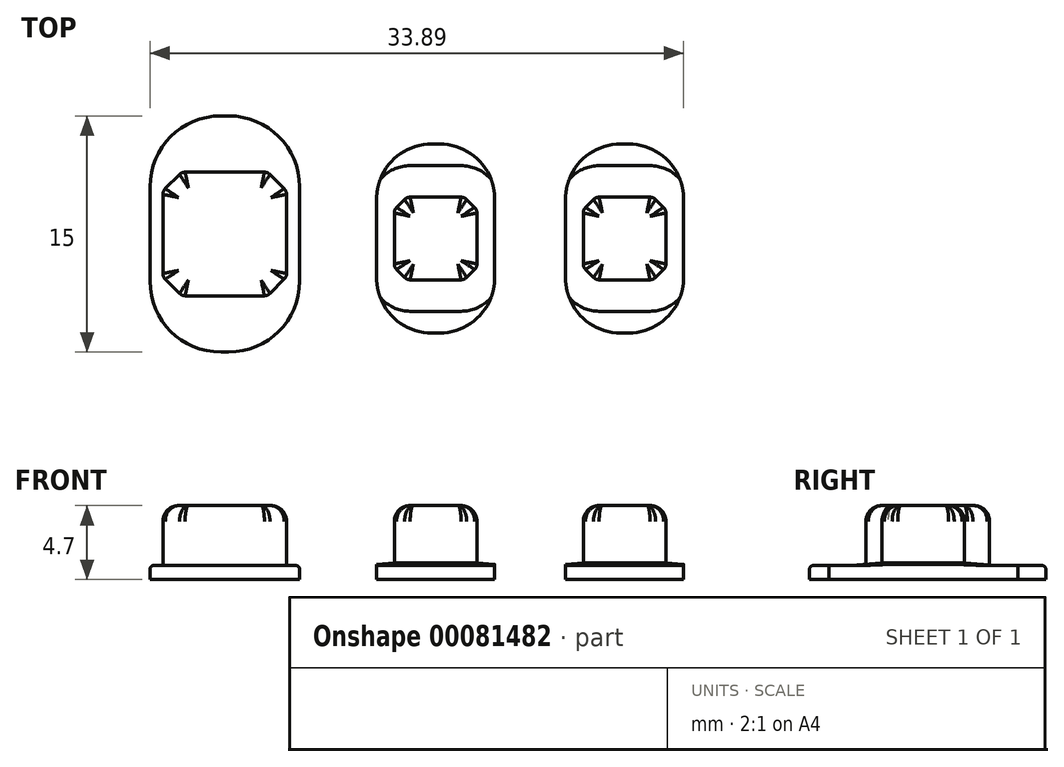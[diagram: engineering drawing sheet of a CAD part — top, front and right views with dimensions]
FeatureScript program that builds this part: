
annotation { "Feature Type Name" : "Feature", "Feature Type Description" : "" }
export const myFeature = defineFeature(function(context is Context, id is Id, definition is map)
    precondition{}
    {
        {
            var Q0;
            Q0=qCreatedBy(makeId("Top.planeOp"),FACE);
            var sketch = newSketch(context, id + "F0", { "sketchPlane" : qUnion([Q0])});
            skLineSegment(sketch, "E0.bottom", {"start": v(-23.44, 11.8) * mm, "end": v(-13.94, 11.8) * mm});
            skLineSegment(sketch, "E0.top", {"start": v(-23.44, -3.2) * mm, "end": v(-13.94, -3.2) * mm});
            skLineSegment(sketch, "E0.left", {"start": v(-23.44, 11.8) * mm, "end": v(-23.44, -3.2) * mm});
            skLineSegment(sketch, "E0.right", {"start": v(-13.94, 11.8) * mm, "end": v(-13.94, -3.2) * mm});
            skLineSegment(sketch, "E1.bottom", {"start": v(-9.05, 10) * mm, "end": v(-1.55, 10) * mm});
            skLineSegment(sketch, "E1.top", {"start": v(-9.05, -2) * mm, "end": v(-1.55, -2) * mm});
            skLineSegment(sketch, "E1.left", {"start": v(-9.05, 10) * mm, "end": v(-9.05, -2) * mm});
            skLineSegment(sketch, "E1.right", {"start": v(-1.55, 10) * mm, "end": v(-1.55, -2) * mm});
            skSolve(sketch);
        }
        {
            var Q0;
            Q0 = qSketchRegion(id + "F0", true);
            extrude(context, id + "F1", {"entities" : qUnion([Q0]), "depth" : .9 * mm});
        }
        {
            var Q0;
            Q0=makeQuery(id+"F1.opExtrude","CAP_FACE",FACE,{"disambiguationData":[OSD([sQuery(id+"F0.wireOp",EDGE,"E0.bottom"),sQuery(id+"F0.wireOp",EDGE,"E0.top"),sQuery(id+"F0.wireOp",EDGE,"E0.left"),sQuery(id+"F0.wireOp",EDGE,"E0.right")])],"isStart":false});
            var sketch = newSketch(context, id + "F2", { "sketchPlane" : qUnion([Q0])});
            skLineSegment(sketch, "E2", {"start": v(-23.44, 4.3) * mm, "end": v(-22.62, 4.3) * mm});
            skLineSegment(sketch, "E3.bottom", {"start": v(-22.62, 8.22) * mm, "end": v(-14.77, 8.22) * mm});
            skLineSegment(sketch, "E3.top", {"start": v(-22.62, 0.37) * mm, "end": v(-14.77, 0.37) * mm});
            skLineSegment(sketch, "E3.left", {"start": v(-22.62, 8.22) * mm, "end": v(-22.62, 0.37) * mm});
            skLineSegment(sketch, "E3.right", {"start": v(-14.77, 8.22) * mm, "end": v(-14.77, 0.37) * mm});
            skPoint(sketch, "E4", {"position": v(-18.7, 0.37) * mm});
            skPoint(sketch, "E5", {"position": v(-22.62, 4.3) * mm});
            skLineSegment(sketch, "E6.trimOffspring", {"start": v(-14.77, 4.3) * mm, "end": v(-13.94, 4.3) * mm});
            skPoint(sketch, "E7.orphan", {"position": v(-18.7, 4.3) * mm});
            skLineSegment(sketch, "E8", {"start": v(-18.7, 0.37) * mm, "end": v(-18.7, 4.3) * mm});
            skSolve(sketch);
        }
        {
            var Q0;
            Q0 = qSketchRegion(id + "F2", true);
            extrude(context, id + "F3", {"entities" : qUnion([Q0]), "operationType" : NewBodyOperationType.ADD, "depth" : 3.8 * mm});
        }
        {
            var Q0;
            Q0=makeQuery(id+"F1.opExtrude","CAP_FACE",FACE,{"disambiguationData":[OSD([sQuery(id+"F0.wireOp",EDGE,"E1.bottom"),sQuery(id+"F0.wireOp",EDGE,"E1.top"),sQuery(id+"F0.wireOp",EDGE,"E1.left"),sQuery(id+"F0.wireOp",EDGE,"E1.right")])],"isStart":false});
            var sketch = newSketch(context, id + "F4", { "sketchPlane" : qUnion([Q0])});
            skPoint(sketch, "E9", {"position": v(-5.3, 10) * mm});
            skPoint(sketch, "E10", {"position": v(-9.05, 4) * mm});
            skLineSegment(sketch, "E11.bottom", {"start": v(-7.92, 6.63) * mm, "end": v(-2.67, 6.63) * mm});
            skLineSegment(sketch, "E11.top", {"start": v(-7.92, 1.38) * mm, "end": v(-2.67, 1.38) * mm});
            skLineSegment(sketch, "E11.left", {"start": v(-7.92, 6.63) * mm, "end": v(-7.92, 1.38) * mm});
            skLineSegment(sketch, "E11.right", {"start": v(-2.67, 6.63) * mm, "end": v(-2.67, 1.38) * mm});
            skLineSegment(sketch, "E12", {"start": v(-9.05, 4) * mm, "end": v(-7.92, 4) * mm});
            skLineSegment(sketch, "E13", {"start": v(-5.3, 10) * mm, "end": v(-5.3, 6.63) * mm});
            skSolve(sketch);
        }
        {
            var Q0;
            Q0 = qSketchRegion(id + "F4", true);
            extrude(context, id + "F5", {"entities" : qUnion([Q0]), "operationType" : NewBodyOperationType.ADD, "depth" : 3.8 * mm});
        }
        {
            var Q0;
            Q0=makeQuery(id+"F1.opExtrude","SWEPT_EDGE",EDGE,{"disambiguationData":[OSD([sQuery(id+"F0.wireOp",EDGE,"E0.top"),sQuery(id+"F0.wireOp",EDGE,"E0.left")])]});
            var Q1;
            Q1=makeQuery(id+"F1.opExtrude","SWEPT_EDGE",EDGE,{"disambiguationData":[OSD([sQuery(id+"F0.wireOp",EDGE,"E0.top"),sQuery(id+"F0.wireOp",EDGE,"E0.right")])]});
            var Q2;
            Q2=makeQuery(id+"F1.opExtrude","SWEPT_EDGE",EDGE,{"disambiguationData":[OSD([sQuery(id+"F0.wireOp",EDGE,"E0.bottom"),sQuery(id+"F0.wireOp",EDGE,"E0.left")])]});
            var Q3;
            Q3=makeQuery(id+"F1.opExtrude","SWEPT_EDGE",EDGE,{"disambiguationData":[OSD([sQuery(id+"F0.wireOp",EDGE,"E0.bottom"),sQuery(id+"F0.wireOp",EDGE,"E0.right")])]});
            fillet(context, id + "F6", {"entities" : qUnion([Q0, Q1, Q2, Q3]), "radius" : 4.5 * mm, "tangentPropagation" : true, "allowEdgeOverflow" : false});
        }
        {
            var Q0;
            Q0=makeQuery(id+"F1.opExtrude","SWEPT_EDGE",EDGE,{"disambiguationData":[OSD([sQuery(id+"F0.wireOp",EDGE,"E1.bottom"),sQuery(id+"F0.wireOp",EDGE,"E1.left")])]});
            var Q1;
            Q1=makeQuery(id+"F1.opExtrude","SWEPT_EDGE",EDGE,{"disambiguationData":[OSD([sQuery(id+"F0.wireOp",EDGE,"E1.bottom"),sQuery(id+"F0.wireOp",EDGE,"E1.right")])]});
            var Q2;
            Q2=makeQuery(id+"F1.opExtrude","SWEPT_EDGE",EDGE,{"disambiguationData":[OSD([sQuery(id+"F0.wireOp",EDGE,"E1.top"),sQuery(id+"F0.wireOp",EDGE,"E1.left")])]});
            var Q3;
            Q3=makeQuery(id+"F1.opExtrude","SWEPT_EDGE",EDGE,{"disambiguationData":[OSD([sQuery(id+"F0.wireOp",EDGE,"E1.top"),sQuery(id+"F0.wireOp",EDGE,"E1.right")])]});
            fillet(context, id + "F7", {"entities" : qUnion([Q0, Q1, Q2, Q3]), "radius" : 3.5 * mm, "tangentPropagation" : true, "allowEdgeOverflow" : false});
        }
        {
            var Q0;
            Q0=makeQuery(id+"F3.opExtrude","SWEPT_EDGE",EDGE,{"disambiguationData":[OSD([sQuery(id+"F2.wireOp",EDGE,"E3.top"),sQuery(id+"F2.wireOp",EDGE,"E3.left")])]});
            var Q1;
            Q1=makeQuery(id+"F3.opExtrude","SWEPT_EDGE",EDGE,{"disambiguationData":[OSD([sQuery(id+"F2.wireOp",EDGE,"E3.top"),sQuery(id+"F2.wireOp",EDGE,"E3.right")])]});
            var Q2;
            Q2=makeQuery(id+"F3.opExtrude","SWEPT_EDGE",EDGE,{"disambiguationData":[OSD([sQuery(id+"F2.wireOp",EDGE,"E3.bottom"),sQuery(id+"F2.wireOp",EDGE,"E3.right")])]});
            var Q3;
            Q3=makeQuery(id+"F3.opExtrude","SWEPT_EDGE",EDGE,{"disambiguationData":[OSD([sQuery(id+"F2.wireOp",EDGE,"E3.bottom"),sQuery(id+"F2.wireOp",EDGE,"E3.left")])]});
            chamfer(context, id + "F8", {"entities" : qUnion([Q0, Q1, Q2, Q3]), "width" : 1.2 * mm, "tangentPropagation" : true});
        }
        {
            var Q0;
            Q0=makeQuery(id+"F5.opExtrude","SWEPT_EDGE",EDGE,{"disambiguationData":[OSD([sQuery(id+"F4.wireOp",EDGE,"E11.top"),sQuery(id+"F4.wireOp",EDGE,"E11.left")])]});
            var Q1;
            Q1=makeQuery(id+"F5.opExtrude","SWEPT_EDGE",EDGE,{"disambiguationData":[OSD([sQuery(id+"F4.wireOp",EDGE,"E11.top"),sQuery(id+"F4.wireOp",EDGE,"E11.right")])]});
            var Q2;
            Q2=makeQuery(id+"F5.opExtrude","SWEPT_EDGE",EDGE,{"disambiguationData":[OSD([sQuery(id+"F4.wireOp",EDGE,"E11.bottom"),sQuery(id+"F4.wireOp",EDGE,"E11.left")])]});
            var Q3;
            Q3=makeQuery(id+"F5.opExtrude","SWEPT_EDGE",EDGE,{"disambiguationData":[OSD([sQuery(id+"F4.wireOp",EDGE,"E11.bottom"),sQuery(id+"F4.wireOp",EDGE,"E11.right")])]});
            chamfer(context, id + "F9", {"entities" : qUnion([Q0, Q1, Q2, Q3]), "width" : .8 * mm, "tangentPropagation" : true});
        }
        {
            var Q0;
            Q0=makeQuery(id+"F3.opExtrude","CAP_FACE",FACE,{"disambiguationData":[OSD([sQuery(id+"F2.wireOp",EDGE,"E3.bottom"),sQuery(id+"F2.wireOp",EDGE,"E3.top"),sQuery(id+"F2.wireOp",EDGE,"E3.left"),sQuery(id+"F2.wireOp",EDGE,"E3.right")])],"isStart":false});
            var Q1;
            Q1=makeQuery(id+"F5.opExtrude","CAP_FACE",FACE,{"disambiguationData":[OSD([sQuery(id+"F4.wireOp",EDGE,"E11.bottom"),sQuery(id+"F4.wireOp",EDGE,"E11.top"),sQuery(id+"F4.wireOp",EDGE,"E11.left"),sQuery(id+"F4.wireOp",EDGE,"E11.right")])],"isStart":false});
            fillet(context, id + "F10", {"entities" : qUnion([Q0, Q1]), "radius" : 1 * mm, "tangentPropagation" : true, "allowEdgeOverflow" : false});
        }
        {
            var Q0;
            {var subQ0=sQuery(id+"F2.wireOp",EDGE,"E3.top");Q0=makeQuery(id+"F8.opChamfer","BLEND_EDGE",EDGE,{"blendedFrom":[makeQuery(id+"F3.opExtrude","SWEPT_EDGE",EDGE,{"disambiguationData":[OSD([subQ0,sQuery(id+"F2.wireOp",EDGE,"E3.left")])]}),makeQuery(id+"F3.opExtrude","SWEPT_FACE",FACE,{"disambiguationData":[OSD([subQ0])]})],"blendedInto":[makeQuery(id+"F3.opExtrude","SWEPT_FACE",FACE,{"disambiguationData":[OSD([subQ0])]})]});}
            var Q1;
            {var subQ0=sQuery(id+"F2.wireOp",EDGE,"E3.left");Q1=makeQuery(id+"F8.opChamfer","BLEND_EDGE",EDGE,{"blendedFrom":[makeQuery(id+"F3.opExtrude","SWEPT_EDGE",EDGE,{"disambiguationData":[OSD([sQuery(id+"F2.wireOp",EDGE,"E3.top"),subQ0])]}),makeQuery(id+"F3.opExtrude","SWEPT_FACE",FACE,{"disambiguationData":[OSD([subQ0])]})],"blendedInto":[makeQuery(id+"F3.opExtrude","SWEPT_FACE",FACE,{"disambiguationData":[OSD([subQ0])]})]});}
            var Q2;
            {var subQ0=sQuery(id+"F2.wireOp",EDGE,"E3.top");Q2=makeQuery(id+"F8.opChamfer","BLEND_EDGE",EDGE,{"blendedFrom":[makeQuery(id+"F3.opExtrude","SWEPT_EDGE",EDGE,{"disambiguationData":[OSD([subQ0,sQuery(id+"F2.wireOp",EDGE,"E3.right")])]}),makeQuery(id+"F3.opExtrude","SWEPT_FACE",FACE,{"disambiguationData":[OSD([subQ0])]})],"blendedInto":[makeQuery(id+"F3.opExtrude","SWEPT_FACE",FACE,{"disambiguationData":[OSD([subQ0])]})]});}
            var Q3;
            {var subQ0=sQuery(id+"F2.wireOp",EDGE,"E3.right");Q3=makeQuery(id+"F8.opChamfer","BLEND_EDGE",EDGE,{"blendedFrom":[makeQuery(id+"F3.opExtrude","SWEPT_EDGE",EDGE,{"disambiguationData":[OSD([sQuery(id+"F2.wireOp",EDGE,"E3.top"),subQ0])]}),makeQuery(id+"F3.opExtrude","SWEPT_FACE",FACE,{"disambiguationData":[OSD([subQ0])]})],"blendedInto":[makeQuery(id+"F3.opExtrude","SWEPT_FACE",FACE,{"disambiguationData":[OSD([subQ0])]})]});}
            var Q4;
            {var subQ0=sQuery(id+"F2.wireOp",EDGE,"E3.right");Q4=makeQuery(id+"F8.opChamfer","BLEND_EDGE",EDGE,{"blendedFrom":[makeQuery(id+"F3.opExtrude","SWEPT_EDGE",EDGE,{"disambiguationData":[OSD([sQuery(id+"F2.wireOp",EDGE,"E3.bottom"),subQ0])]}),makeQuery(id+"F3.opExtrude","SWEPT_FACE",FACE,{"disambiguationData":[OSD([subQ0])]})],"blendedInto":[makeQuery(id+"F3.opExtrude","SWEPT_FACE",FACE,{"disambiguationData":[OSD([subQ0])]})]});}
            var Q5;
            {var subQ0=sQuery(id+"F2.wireOp",EDGE,"E3.bottom");Q5=makeQuery(id+"F8.opChamfer","BLEND_EDGE",EDGE,{"blendedFrom":[makeQuery(id+"F3.opExtrude","SWEPT_EDGE",EDGE,{"disambiguationData":[OSD([subQ0,sQuery(id+"F2.wireOp",EDGE,"E3.right")])]}),makeQuery(id+"F3.opExtrude","SWEPT_FACE",FACE,{"disambiguationData":[OSD([subQ0])]})],"blendedInto":[makeQuery(id+"F3.opExtrude","SWEPT_FACE",FACE,{"disambiguationData":[OSD([subQ0])]})]});}
            var Q6;
            {var subQ0=sQuery(id+"F2.wireOp",EDGE,"E3.bottom");Q6=makeQuery(id+"F8.opChamfer","BLEND_EDGE",EDGE,{"blendedFrom":[makeQuery(id+"F3.opExtrude","SWEPT_EDGE",EDGE,{"disambiguationData":[OSD([subQ0,sQuery(id+"F2.wireOp",EDGE,"E3.left")])]}),makeQuery(id+"F3.opExtrude","SWEPT_FACE",FACE,{"disambiguationData":[OSD([subQ0])]})],"blendedInto":[makeQuery(id+"F3.opExtrude","SWEPT_FACE",FACE,{"disambiguationData":[OSD([subQ0])]})]});}
            var Q7;
            {var subQ0=sQuery(id+"F2.wireOp",EDGE,"E3.left");Q7=makeQuery(id+"F8.opChamfer","BLEND_EDGE",EDGE,{"blendedFrom":[makeQuery(id+"F3.opExtrude","SWEPT_EDGE",EDGE,{"disambiguationData":[OSD([sQuery(id+"F2.wireOp",EDGE,"E3.bottom"),subQ0])]}),makeQuery(id+"F3.opExtrude","SWEPT_FACE",FACE,{"disambiguationData":[OSD([subQ0])]})],"blendedInto":[makeQuery(id+"F3.opExtrude","SWEPT_FACE",FACE,{"disambiguationData":[OSD([subQ0])]})]});}
            var Q8;
            {var subQ0=sQuery(id+"F4.wireOp",EDGE,"E11.top");Q8=makeQuery(id+"F8.opChamfer","BLEND_EDGE",EDGE,{"blendedFrom":[makeQuery(id+"F5.opExtrude","SWEPT_EDGE",EDGE,{"disambiguationData":[OSD([subQ0,sQuery(id+"F4.wireOp",EDGE,"E11.left")])]}),makeQuery(id+"F5.opExtrude","SWEPT_FACE",FACE,{"disambiguationData":[OSD([subQ0])]})],"blendedInto":[makeQuery(id+"F5.opExtrude","SWEPT_FACE",FACE,{"disambiguationData":[OSD([subQ0])]})]});}
            var Q9;
            {var subQ0=sQuery(id+"F4.wireOp",EDGE,"E11.top");Q9=makeQuery(id+"F8.opChamfer","BLEND_EDGE",EDGE,{"blendedFrom":[makeQuery(id+"F5.opExtrude","SWEPT_EDGE",EDGE,{"disambiguationData":[OSD([subQ0,sQuery(id+"F4.wireOp",EDGE,"E11.right")])]}),makeQuery(id+"F5.opExtrude","SWEPT_FACE",FACE,{"disambiguationData":[OSD([subQ0])]})],"blendedInto":[makeQuery(id+"F5.opExtrude","SWEPT_FACE",FACE,{"disambiguationData":[OSD([subQ0])]})]});}
            var Q10;
            {var subQ0=sQuery(id+"F4.wireOp",EDGE,"E11.right");Q10=makeQuery(id+"F8.opChamfer","BLEND_EDGE",EDGE,{"blendedFrom":[makeQuery(id+"F5.opExtrude","SWEPT_EDGE",EDGE,{"disambiguationData":[OSD([sQuery(id+"F4.wireOp",EDGE,"E11.top"),subQ0])]}),makeQuery(id+"F5.opExtrude","SWEPT_FACE",FACE,{"disambiguationData":[OSD([subQ0])]})],"blendedInto":[makeQuery(id+"F5.opExtrude","SWEPT_FACE",FACE,{"disambiguationData":[OSD([subQ0])]})]});}
            var Q11;
            {var subQ0=sQuery(id+"F4.wireOp",EDGE,"E11.right");Q11=makeQuery(id+"F8.opChamfer","BLEND_EDGE",EDGE,{"blendedFrom":[makeQuery(id+"F5.opExtrude","SWEPT_EDGE",EDGE,{"disambiguationData":[OSD([sQuery(id+"F4.wireOp",EDGE,"E11.bottom"),subQ0])]}),makeQuery(id+"F5.opExtrude","SWEPT_FACE",FACE,{"disambiguationData":[OSD([subQ0])]})],"blendedInto":[makeQuery(id+"F5.opExtrude","SWEPT_FACE",FACE,{"disambiguationData":[OSD([subQ0])]})]});}
            var Q12;
            {var subQ0=sQuery(id+"F4.wireOp",EDGE,"E11.bottom");Q12=makeQuery(id+"F8.opChamfer","BLEND_EDGE",EDGE,{"blendedFrom":[makeQuery(id+"F5.opExtrude","SWEPT_EDGE",EDGE,{"disambiguationData":[OSD([subQ0,sQuery(id+"F4.wireOp",EDGE,"E11.right")])]}),makeQuery(id+"F5.opExtrude","SWEPT_FACE",FACE,{"disambiguationData":[OSD([subQ0])]})],"blendedInto":[makeQuery(id+"F5.opExtrude","SWEPT_FACE",FACE,{"disambiguationData":[OSD([subQ0])]})]});}
            var Q13;
            {var subQ0=sQuery(id+"F4.wireOp",EDGE,"E11.bottom");Q13=makeQuery(id+"F8.opChamfer","BLEND_EDGE",EDGE,{"blendedFrom":[makeQuery(id+"F5.opExtrude","SWEPT_EDGE",EDGE,{"disambiguationData":[OSD([subQ0,sQuery(id+"F4.wireOp",EDGE,"E11.left")])]}),makeQuery(id+"F5.opExtrude","SWEPT_FACE",FACE,{"disambiguationData":[OSD([subQ0])]})],"blendedInto":[makeQuery(id+"F5.opExtrude","SWEPT_FACE",FACE,{"disambiguationData":[OSD([subQ0])]})]});}
            var Q14;
            {var subQ0=sQuery(id+"F4.wireOp",EDGE,"E11.left");Q14=makeQuery(id+"F8.opChamfer","BLEND_EDGE",EDGE,{"blendedFrom":[makeQuery(id+"F5.opExtrude","SWEPT_EDGE",EDGE,{"disambiguationData":[OSD([sQuery(id+"F4.wireOp",EDGE,"E11.bottom"),subQ0])]}),makeQuery(id+"F5.opExtrude","SWEPT_FACE",FACE,{"disambiguationData":[OSD([subQ0])]})],"blendedInto":[makeQuery(id+"F5.opExtrude","SWEPT_FACE",FACE,{"disambiguationData":[OSD([subQ0])]})]});}
            var Q15;
            {var subQ0=sQuery(id+"F4.wireOp",EDGE,"E11.left");Q15=makeQuery(id+"F8.opChamfer","BLEND_EDGE",EDGE,{"blendedFrom":[makeQuery(id+"F5.opExtrude","SWEPT_EDGE",EDGE,{"disambiguationData":[OSD([sQuery(id+"F4.wireOp",EDGE,"E11.top"),subQ0])]}),makeQuery(id+"F5.opExtrude","SWEPT_FACE",FACE,{"disambiguationData":[OSD([subQ0])]})],"blendedInto":[makeQuery(id+"F5.opExtrude","SWEPT_FACE",FACE,{"disambiguationData":[OSD([subQ0])]})]});}
            var Q16;
            {var subQ0=sQuery(id+"F4.wireOp",EDGE,"E11.top");Q16=makeQuery(id+"F9.opChamfer","BLEND_EDGE",EDGE,{"blendedFrom":[makeQuery(id+"F5.opExtrude","SWEPT_EDGE",EDGE,{"disambiguationData":[OSD([subQ0,sQuery(id+"F4.wireOp",EDGE,"E11.left")])]}),makeQuery(id+"F5.opExtrude","SWEPT_FACE",FACE,{"disambiguationData":[OSD([subQ0])]})],"blendedInto":[makeQuery(id+"F5.opExtrude","SWEPT_FACE",FACE,{"disambiguationData":[OSD([subQ0])]})]});}
            var Q17;
            {var subQ0=sQuery(id+"F4.wireOp",EDGE,"E11.top");Q17=makeQuery(id+"F9.opChamfer","BLEND_EDGE",EDGE,{"blendedFrom":[makeQuery(id+"F5.opExtrude","SWEPT_EDGE",EDGE,{"disambiguationData":[OSD([subQ0,sQuery(id+"F4.wireOp",EDGE,"E11.right")])]}),makeQuery(id+"F5.opExtrude","SWEPT_FACE",FACE,{"disambiguationData":[OSD([subQ0])]})],"blendedInto":[makeQuery(id+"F5.opExtrude","SWEPT_FACE",FACE,{"disambiguationData":[OSD([subQ0])]})]});}
            var Q18;
            {var subQ0=sQuery(id+"F4.wireOp",EDGE,"E11.right");Q18=makeQuery(id+"F9.opChamfer","BLEND_EDGE",EDGE,{"blendedFrom":[makeQuery(id+"F5.opExtrude","SWEPT_EDGE",EDGE,{"disambiguationData":[OSD([sQuery(id+"F4.wireOp",EDGE,"E11.top"),subQ0])]}),makeQuery(id+"F5.opExtrude","SWEPT_FACE",FACE,{"disambiguationData":[OSD([subQ0])]})],"blendedInto":[makeQuery(id+"F5.opExtrude","SWEPT_FACE",FACE,{"disambiguationData":[OSD([subQ0])]})]});}
            var Q19;
            {var subQ0=sQuery(id+"F4.wireOp",EDGE,"E11.right");Q19=makeQuery(id+"F9.opChamfer","BLEND_EDGE",EDGE,{"blendedFrom":[makeQuery(id+"F5.opExtrude","SWEPT_EDGE",EDGE,{"disambiguationData":[OSD([sQuery(id+"F4.wireOp",EDGE,"E11.bottom"),subQ0])]}),makeQuery(id+"F5.opExtrude","SWEPT_FACE",FACE,{"disambiguationData":[OSD([subQ0])]})],"blendedInto":[makeQuery(id+"F5.opExtrude","SWEPT_FACE",FACE,{"disambiguationData":[OSD([subQ0])]})]});}
            var Q20;
            {var subQ0=sQuery(id+"F4.wireOp",EDGE,"E11.bottom");Q20=makeQuery(id+"F9.opChamfer","BLEND_EDGE",EDGE,{"blendedFrom":[makeQuery(id+"F5.opExtrude","SWEPT_EDGE",EDGE,{"disambiguationData":[OSD([subQ0,sQuery(id+"F4.wireOp",EDGE,"E11.right")])]}),makeQuery(id+"F5.opExtrude","SWEPT_FACE",FACE,{"disambiguationData":[OSD([subQ0])]})],"blendedInto":[makeQuery(id+"F5.opExtrude","SWEPT_FACE",FACE,{"disambiguationData":[OSD([subQ0])]})]});}
            var Q21;
            {var subQ0=sQuery(id+"F4.wireOp",EDGE,"E11.left");Q21=makeQuery(id+"F9.opChamfer","BLEND_EDGE",EDGE,{"blendedFrom":[makeQuery(id+"F5.opExtrude","SWEPT_EDGE",EDGE,{"disambiguationData":[OSD([sQuery(id+"F4.wireOp",EDGE,"E11.top"),subQ0])]}),makeQuery(id+"F5.opExtrude","SWEPT_FACE",FACE,{"disambiguationData":[OSD([subQ0])]})],"blendedInto":[makeQuery(id+"F5.opExtrude","SWEPT_FACE",FACE,{"disambiguationData":[OSD([subQ0])]})]});}
            var Q22;
            {var subQ0=sQuery(id+"F4.wireOp",EDGE,"E11.left");Q22=makeQuery(id+"F9.opChamfer","BLEND_EDGE",EDGE,{"blendedFrom":[makeQuery(id+"F5.opExtrude","SWEPT_EDGE",EDGE,{"disambiguationData":[OSD([sQuery(id+"F4.wireOp",EDGE,"E11.bottom"),subQ0])]}),makeQuery(id+"F5.opExtrude","SWEPT_FACE",FACE,{"disambiguationData":[OSD([subQ0])]})],"blendedInto":[makeQuery(id+"F5.opExtrude","SWEPT_FACE",FACE,{"disambiguationData":[OSD([subQ0])]})]});}
            var Q23;
            {var subQ0=sQuery(id+"F4.wireOp",EDGE,"E11.bottom");Q23=makeQuery(id+"F9.opChamfer","BLEND_EDGE",EDGE,{"blendedFrom":[makeQuery(id+"F5.opExtrude","SWEPT_EDGE",EDGE,{"disambiguationData":[OSD([subQ0,sQuery(id+"F4.wireOp",EDGE,"E11.left")])]}),makeQuery(id+"F5.opExtrude","SWEPT_FACE",FACE,{"disambiguationData":[OSD([subQ0])]})],"blendedInto":[makeQuery(id+"F5.opExtrude","SWEPT_FACE",FACE,{"disambiguationData":[OSD([subQ0])]})]});}
            fillet(context, id + "F11", {"entities" : qUnion([Q0, Q1, Q2, Q3, Q4, Q5, Q6, Q7, Q8, Q9, Q10, Q11, Q12, Q13, Q14, Q15, Q16, Q17, Q18, Q19, Q20, Q21, Q22, Q23]), "radius" : .5 * mm, "tangentPropagation" : true, "allowEdgeOverflow" : false});
        }
        {
            var Q0;
            Q0=makeQuery(id+"F3.opExtrude","CAP_EDGE",EDGE,{"disambiguationData":[OSD([sQuery(id+"F2.wireOp",EDGE,"E3.top")])],"isStart":true});
            var Q1;
            Q1=makeQuery(id+"F5.opExtrude","CAP_EDGE",EDGE,{"disambiguationData":[OSD([sQuery(id+"F4.wireOp",EDGE,"E11.top")])],"isStart":true});
            var Q2;
            Q2=makeQuery(id+"F9.opChamfer","BLEND_EDGE",EDGE,{"blendedFrom":[makeQuery(id+"F5.opExtrude","SWEPT_EDGE",EDGE,{"disambiguationData":[OSD([sQuery(id+"F4.wireOp",EDGE,"E11.top"),sQuery(id+"F4.wireOp",EDGE,"E11.left")])]}),makeQuery(id+"F1.opExtrude","CAP_FACE",FACE,{"disambiguationData":[OSD([sQuery(id+"F0.wireOp",EDGE,"E1.bottom"),sQuery(id+"F0.wireOp",EDGE,"E1.top"),sQuery(id+"F0.wireOp",EDGE,"E1.left"),sQuery(id+"F0.wireOp",EDGE,"E1.right")])],"isStart":false})],"blendedInto":[makeQuery(id+"F1.opExtrude","CAP_FACE",FACE,{"disambiguationData":[OSD([sQuery(id+"F0.wireOp",EDGE,"E1.bottom"),sQuery(id+"F0.wireOp",EDGE,"E1.top"),sQuery(id+"F0.wireOp",EDGE,"E1.left"),sQuery(id+"F0.wireOp",EDGE,"E1.right")])],"isStart":false})]});
            var Q3;
            Q3=makeQuery(id+"F5.opExtrude","CAP_EDGE",EDGE,{"disambiguationData":[OSD([sQuery(id+"F4.wireOp",EDGE,"E11.left")])],"isStart":true});
            var Q4;
            Q4=makeQuery(id+"F9.opChamfer","BLEND_EDGE",EDGE,{"blendedFrom":[makeQuery(id+"F5.opExtrude","SWEPT_EDGE",EDGE,{"disambiguationData":[OSD([sQuery(id+"F4.wireOp",EDGE,"E11.top"),sQuery(id+"F4.wireOp",EDGE,"E11.right")])]}),makeQuery(id+"F1.opExtrude","CAP_FACE",FACE,{"disambiguationData":[OSD([sQuery(id+"F0.wireOp",EDGE,"E1.bottom"),sQuery(id+"F0.wireOp",EDGE,"E1.top"),sQuery(id+"F0.wireOp",EDGE,"E1.left"),sQuery(id+"F0.wireOp",EDGE,"E1.right")])],"isStart":false})],"blendedInto":[makeQuery(id+"F1.opExtrude","CAP_FACE",FACE,{"disambiguationData":[OSD([sQuery(id+"F0.wireOp",EDGE,"E1.bottom"),sQuery(id+"F0.wireOp",EDGE,"E1.top"),sQuery(id+"F0.wireOp",EDGE,"E1.left"),sQuery(id+"F0.wireOp",EDGE,"E1.right")])],"isStart":false})]});
            var Q5;
            Q5=makeQuery(id+"F5.opExtrude","CAP_EDGE",EDGE,{"disambiguationData":[OSD([sQuery(id+"F4.wireOp",EDGE,"E11.right")])],"isStart":true});
            var Q6;
            Q6=makeQuery(id+"F9.opChamfer","BLEND_EDGE",EDGE,{"blendedFrom":[makeQuery(id+"F5.opExtrude","SWEPT_EDGE",EDGE,{"disambiguationData":[OSD([sQuery(id+"F4.wireOp",EDGE,"E11.bottom"),sQuery(id+"F4.wireOp",EDGE,"E11.right")])]}),makeQuery(id+"F1.opExtrude","CAP_FACE",FACE,{"disambiguationData":[OSD([sQuery(id+"F0.wireOp",EDGE,"E1.bottom"),sQuery(id+"F0.wireOp",EDGE,"E1.top"),sQuery(id+"F0.wireOp",EDGE,"E1.left"),sQuery(id+"F0.wireOp",EDGE,"E1.right")])],"isStart":false})],"blendedInto":[makeQuery(id+"F1.opExtrude","CAP_FACE",FACE,{"disambiguationData":[OSD([sQuery(id+"F0.wireOp",EDGE,"E1.bottom"),sQuery(id+"F0.wireOp",EDGE,"E1.top"),sQuery(id+"F0.wireOp",EDGE,"E1.left"),sQuery(id+"F0.wireOp",EDGE,"E1.right")])],"isStart":false})]});
            var Q7;
            Q7=makeQuery(id+"F5.opExtrude","CAP_EDGE",EDGE,{"disambiguationData":[OSD([sQuery(id+"F4.wireOp",EDGE,"E11.bottom")])],"isStart":true});
            var Q8;
            Q8=makeQuery(id+"F9.opChamfer","BLEND_EDGE",EDGE,{"blendedFrom":[makeQuery(id+"F5.opExtrude","SWEPT_EDGE",EDGE,{"disambiguationData":[OSD([sQuery(id+"F4.wireOp",EDGE,"E11.bottom"),sQuery(id+"F4.wireOp",EDGE,"E11.left")])]}),makeQuery(id+"F1.opExtrude","CAP_FACE",FACE,{"disambiguationData":[OSD([sQuery(id+"F0.wireOp",EDGE,"E1.bottom"),sQuery(id+"F0.wireOp",EDGE,"E1.top"),sQuery(id+"F0.wireOp",EDGE,"E1.left"),sQuery(id+"F0.wireOp",EDGE,"E1.right")])],"isStart":false})],"blendedInto":[makeQuery(id+"F1.opExtrude","CAP_FACE",FACE,{"disambiguationData":[OSD([sQuery(id+"F0.wireOp",EDGE,"E1.bottom"),sQuery(id+"F0.wireOp",EDGE,"E1.top"),sQuery(id+"F0.wireOp",EDGE,"E1.left"),sQuery(id+"F0.wireOp",EDGE,"E1.right")])],"isStart":false})]});
            chamfer(context, id + "F12", {"entities" : qUnion([Q0, Q1, Q2, Q3, Q4, Q5, Q6, Q7, Q8]), "chamferType" : ChamferType.TWO_OFFSETS, "width1" : 2 * mm, "oppositeDirection" : false, "width2" : .15 * mm, "tangentPropagation" : true});
        }
        {
            var Q0;
            Q0=makeQuery(id+"F1.opExtrude","SWEPT_BODY",BODY,{"disambiguationData":[OSD([sQuery(id+"F0.wireOp",EDGE,"E1.bottom"),sQuery(id+"F0.wireOp",EDGE,"E1.top"),sQuery(id+"F0.wireOp",EDGE,"E1.left"),sQuery(id+"F0.wireOp",EDGE,"E1.right")])]});
            transform(context, id + "F13", {"entities" : qUnion([Q0]), "transformType" : TransformType.TRANSLATION_3D, "dx" : 12 * mm, "dy" : 0 * mm, "dz" : 0 * mm, "makeCopy" : true});
        }
        {
            var Q0;
            {var subQ0=sQuery(id+"F0.wireOp",EDGE,"E0.left");var subQ1=sQuery(id+"F0.wireOp",EDGE,"E0.top");Q0=makeQuery(id+"F6.opFillet","BLEND_EDGE",EDGE,{"blendedFrom":[makeQuery(id+"F1.opExtrude","SWEPT_EDGE",EDGE,{"disambiguationData":[OSD([subQ1,subQ0])]}),makeQuery(id+"F1.opExtrude","CAP_FACE",FACE,{"disambiguationData":[OSD([sQuery(id+"F0.wireOp",EDGE,"E0.bottom"),subQ1,subQ0,sQuery(id+"F0.wireOp",EDGE,"E0.right")])],"isStart":false})],"blendedInto":[makeQuery(id+"F1.opExtrude","CAP_FACE",FACE,{"disambiguationData":[OSD([sQuery(id+"F0.wireOp",EDGE,"E0.bottom"),subQ1,subQ0,sQuery(id+"F0.wireOp",EDGE,"E0.right")])],"isStart":false})]});}
            var Q1;
            {var subQ0=sQuery(id+"F0.wireOp",EDGE,"E1.left");var subQ1=sQuery(id+"F0.wireOp",EDGE,"E1.top");Q1=makeQuery(id+"F7.opFillet","BLEND_EDGE",EDGE,{"blendedFrom":[makeQuery(id+"F1.opExtrude","SWEPT_EDGE",EDGE,{"disambiguationData":[OSD([subQ1,subQ0])]}),makeQuery(id+"F1.opExtrude","CAP_FACE",FACE,{"disambiguationData":[OSD([sQuery(id+"F0.wireOp",EDGE,"E1.bottom"),subQ1,subQ0,sQuery(id+"F0.wireOp",EDGE,"E1.right")])],"isStart":false})],"blendedInto":[makeQuery(id+"F1.opExtrude","CAP_FACE",FACE,{"disambiguationData":[OSD([sQuery(id+"F0.wireOp",EDGE,"E1.bottom"),subQ1,subQ0,sQuery(id+"F0.wireOp",EDGE,"E1.right")])],"isStart":false})]});}
            var Q2;
            {var subQ0=sQuery(id+"F0.wireOp",EDGE,"E1.left");var subQ1=sQuery(id+"F0.wireOp",EDGE,"E1.top");Q2=makeQuery(id+"F13.opPattern","COPY",EDGE,{"derivedFrom":makeQuery(id+"F7.opFillet","BLEND_EDGE",EDGE,{"blendedFrom":[makeQuery(id+"F1.opExtrude","SWEPT_EDGE",EDGE,{"disambiguationData":[OSD([subQ1,subQ0])]}),makeQuery(id+"F1.opExtrude","CAP_FACE",FACE,{"disambiguationData":[OSD([sQuery(id+"F0.wireOp",EDGE,"E1.bottom"),subQ1,subQ0,sQuery(id+"F0.wireOp",EDGE,"E1.right")])],"isStart":false})],"blendedInto":[makeQuery(id+"F1.opExtrude","CAP_FACE",FACE,{"disambiguationData":[OSD([sQuery(id+"F0.wireOp",EDGE,"E1.bottom"),subQ1,subQ0,sQuery(id+"F0.wireOp",EDGE,"E1.right")])],"isStart":false})]}),"instanceName":"1"});}
            fillet(context, id + "F14", {"entities" : qUnion([Q0, Q1, Q2]), "radius" : .25 * mm, "tangentPropagation" : true, "allowEdgeOverflow" : false});
        }
    });
